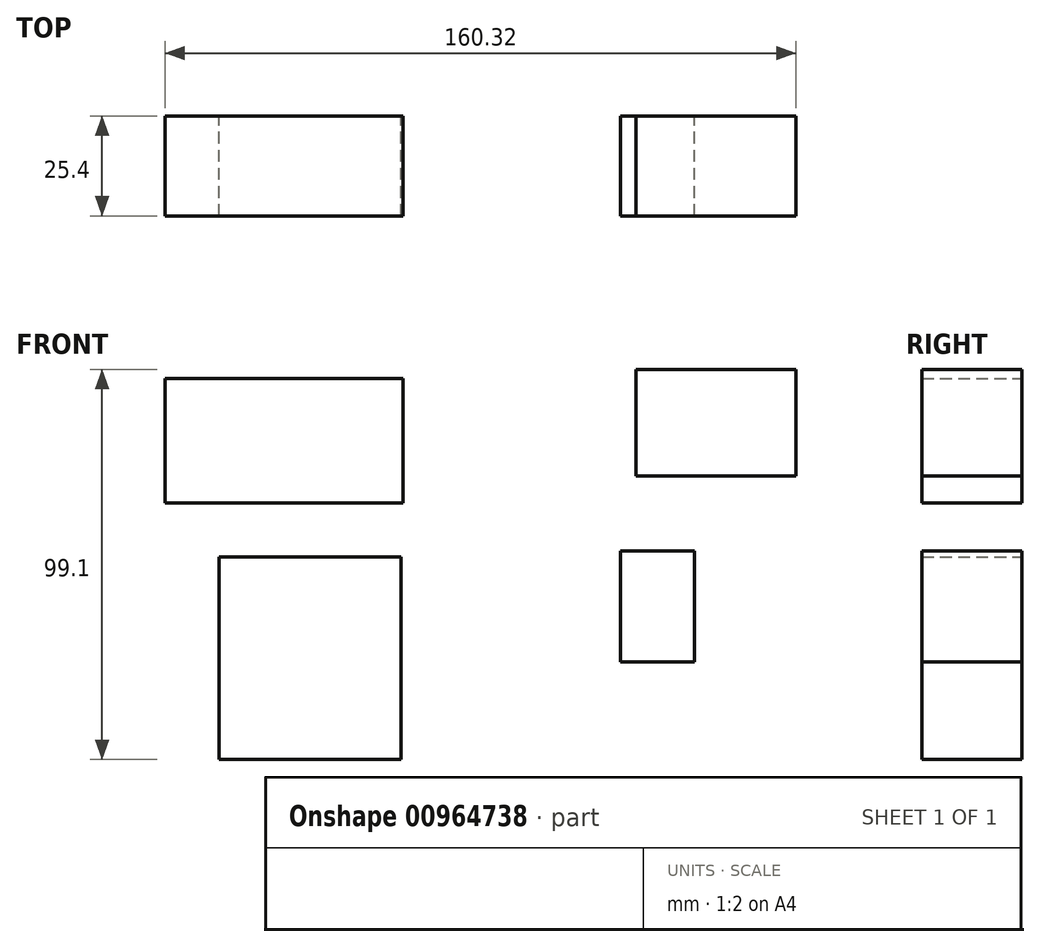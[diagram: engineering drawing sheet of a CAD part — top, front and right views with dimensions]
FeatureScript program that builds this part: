
annotation { "Feature Type Name" : "Feature", "Feature Type Description" : "" }
export const myFeature = defineFeature(function(context is Context, id is Id, definition is map)
    precondition{}
    {
        {
            var Q0;
            Q0=qCreatedBy(makeId("Front.planeOp"),FACE);
            var sketch = newSketch(context, id + "F0", { "sketchPlane" : qUnion([Q0])});
            skLineSegment(sketch, "E0.bottom", {"start": v(-87.3, 44.78) * mm, "end": v(-41.15, 44.78) * mm});
            skLineSegment(sketch, "E0.top", {"start": v(-87.3, -6.65) * mm, "end": v(-41.15, -6.65) * mm});
            skLineSegment(sketch, "E0.left", {"start": v(-87.3, 44.78) * mm, "end": v(-87.3, -6.65) * mm});
            skLineSegment(sketch, "E0.right", {"start": v(-41.15, 44.78) * mm, "end": v(-41.15, -6.65) * mm});
            skLineSegment(sketch, "E1.bottom", {"start": v(14.55, 46.29) * mm, "end": v(33.37, 46.29) * mm});
            skLineSegment(sketch, "E1.top", {"start": v(14.55, 18.19) * mm, "end": v(33.37, 18.19) * mm});
            skLineSegment(sketch, "E1.left", {"start": v(14.55, 46.29) * mm, "end": v(14.55, 18.19) * mm});
            skLineSegment(sketch, "E1.right", {"start": v(33.37, 46.29) * mm, "end": v(33.37, 18.19) * mm});
            skLineSegment(sketch, "E2.bottom", {"start": v(18.57, 92.45) * mm, "end": v(59.2, 92.45) * mm});
            skLineSegment(sketch, "E2.top", {"start": v(18.57, 65.36) * mm, "end": v(59.2, 65.36) * mm});
            skLineSegment(sketch, "E2.left", {"start": v(18.57, 92.45) * mm, "end": v(18.57, 65.36) * mm});
            skLineSegment(sketch, "E2.right", {"start": v(59.2, 92.45) * mm, "end": v(59.2, 65.36) * mm});
            skLineSegment(sketch, "E3.bottom", {"start": v(-101.1, 90.2) * mm, "end": v(-40.64, 90.2) * mm});
            skLineSegment(sketch, "E3.top", {"start": v(-101.1, 58.58) * mm, "end": v(-40.64, 58.58) * mm});
            skLineSegment(sketch, "E3.left", {"start": v(-101.1, 90.2) * mm, "end": v(-101.1, 58.58) * mm});
            skLineSegment(sketch, "E3.right", {"start": v(-40.64, 90.2) * mm, "end": v(-40.64, 58.58) * mm});
            skSolve(sketch);
        }
        {
            var Q0;
            Q0 = qSketchRegion(id + "F0", true);
            extrude(context, id + "F1", {"entities" : qUnion([Q0]), "depth" : 25.4 * mm, "offsetDistance" : 25.4 * mm});
        }
    });
